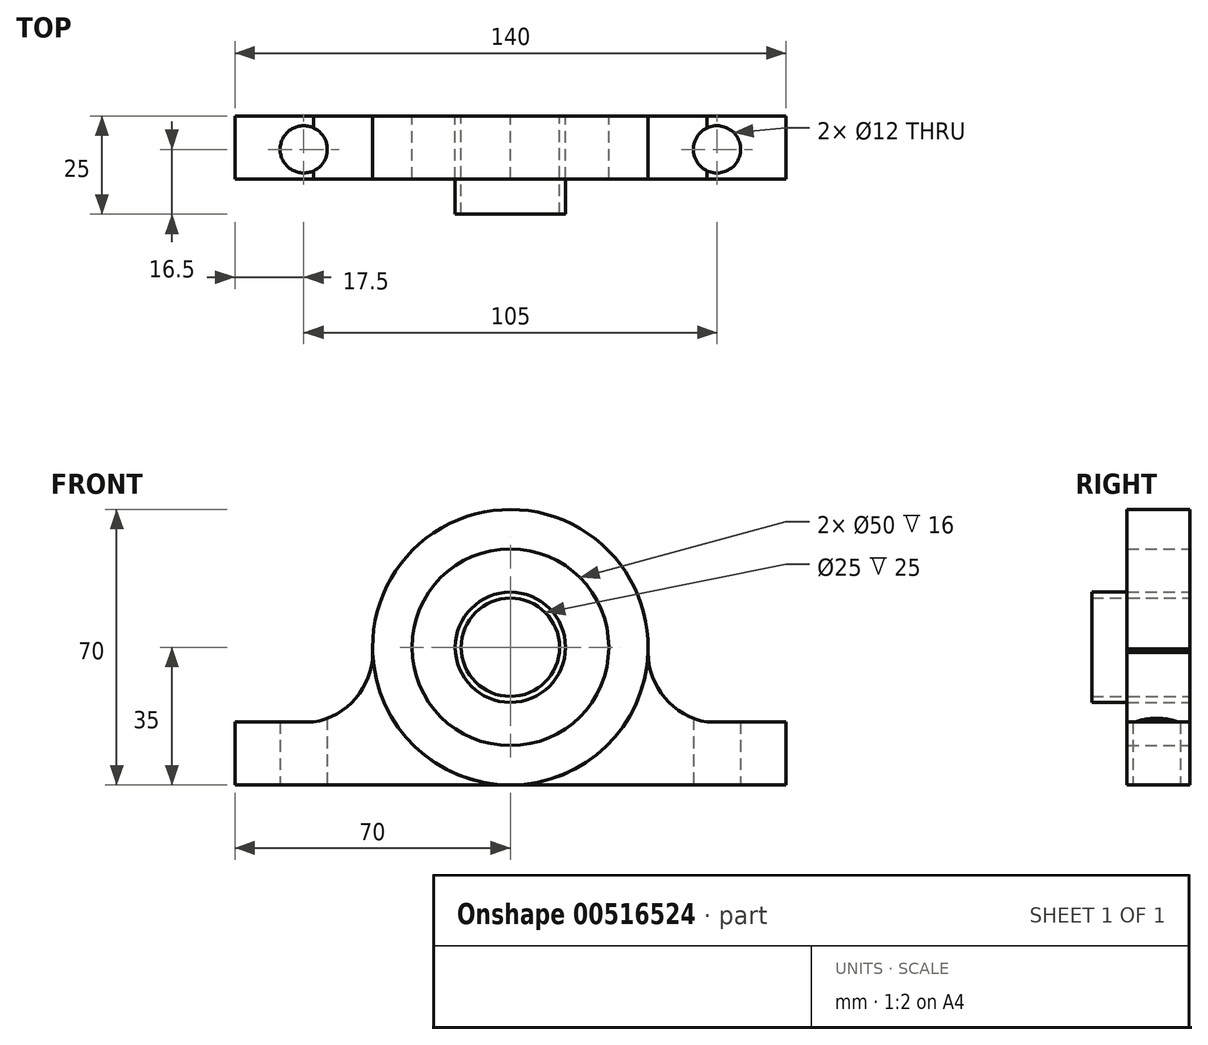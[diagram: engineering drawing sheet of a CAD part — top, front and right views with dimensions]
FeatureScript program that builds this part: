
annotation { "Feature Type Name" : "Feature", "Feature Type Description" : "" }
export const myFeature = defineFeature(function(context is Context, id is Id, definition is map)
    precondition{}
    {
        {
            var Q0;
            Q0=qCreatedBy(makeId("Front.planeOp"),FACE);
            var sketch = newSketch(context, id + "F0", { "sketchPlane" : qUnion([Q0])});
            skLineSegment(sketch, "E0", {"start": v(0, 74.96) * mm, "end": v(0, -75.16) * mm, "construction": true});
            skLineSegment(sketch, "E1", {"start": v(-74.87, 0) * mm, "end": v(74.87, 0) * mm, "construction": true});
            skPoint(sketch, "E2.middle", {"position": v(0, 0) * mm});
            skLineSegment(sketch, "E3.bottom", {"start": v(-70, -8) * mm, "end": v(70, -8) * mm});
            skLineSegment(sketch, "E3.top", {"start": v(-70, 8) * mm, "end": v(70, 8) * mm});
            skLineSegment(sketch, "E3.left", {"start": v(-70, -8) * mm, "end": v(-70, 8) * mm});
            skLineSegment(sketch, "E3.right", {"start": v(70, -8) * mm, "end": v(70, 8) * mm});
            skCircle(sketch, "E4", {"center": v(0, 27) * mm, "radius": 35 * mm});
            skArc(sketch, "E5", {"start": v(-50, 8) * mm, "mid": v(-38.9, 14.54) * mm, "end": v(-35, 26.83) * mm});
            skArc(sketch, "E6", {"start": v(35, 26.62) * mm, "mid": v(38.96, 14.46) * mm, "end": v(50, 8) * mm});
            skCircle(sketch, "E7", {"center": v(0, 27) * mm, "radius": 12.5 * mm});
            skCircle(sketch, "E8", {"center": v(0, 27) * mm, "radius": 14 * mm});
            skCircle(sketch, "E9", {"center": v(0, 27) * mm, "radius": 25 * mm});
            skCircle(sketch, "E10", {"center": v(0, 27) * mm, "radius": 23.5 * mm});
            skSolve(sketch);
        }
        {
            var Q0;
            {var subQ0=sQuery(id+"F0.wireOp",EDGE,"E3.right");Q0=makeQuery(id+"F0.imprint","IMPRINT",FACE,{"disambiguationData":[TD([[makeQuery(id+"F0.imprint","IMPRINT",EDGE,{"derivedFrom":subQ0}),1.0]])]});}
            var Q1;
            {var subQ0=sQuery(id+"F0.wireOp",EDGE,"E3.left");Q1=makeQuery(id+"F0.imprint","IMPRINT",FACE,{"disambiguationData":[TD([[makeQuery(id+"F0.imprint","IMPRINT",EDGE,{"derivedFrom":subQ0}),-1.0]])]});}
            var Q2;
            {var subQ0=sQuery(id+"F0.wireOp",EDGE,"E5");var subQ1=sQuery(id+"F0.wireOp",EDGE,"E3.top");var subQ2=makeQuery(id+"F0.imprint","INTERSECT",VERTEX,{"derivedFrom":[subQ1,subQ0]});Q2=makeQuery(id+"F0.imprint","IMPRINT",FACE,{"disambiguationData":[TD([[makeQuery(id+"F0.imprint","IMPRINT",EDGE,{"disambiguationData":[TD([[subQ2,-1.0]])],"derivedFrom":subQ1}),1.0]])]});}
            var Q3;
            {var subQ0=sQuery(id+"F0.wireOp",EDGE,"E6");var subQ1=sQuery(id+"F0.wireOp",EDGE,"E3.top");var subQ2=makeQuery(id+"F0.imprint","INTERSECT",VERTEX,{"derivedFrom":[subQ1,subQ0]});Q3=makeQuery(id+"F0.imprint","IMPRINT",FACE,{"disambiguationData":[TD([[makeQuery(id+"F0.imprint","IMPRINT",EDGE,{"disambiguationData":[TD([[subQ2,1.0]])],"derivedFrom":subQ1}),1.0]])]});}
            extrude(context, id + "F1", {"entities" : qUnion([Q0, Q1, Q2, Q3]), "depth" : 16 * mm, "offsetDistance" : 25 * mm});
        }
        {
            var Q0;
            {var subQ0=sQuery(id+"F0.wireOp",EDGE,"E4");var subQ2=sQuery(id+"F0.wireOp",EDGE,"E3.top");var subQ4=makeQuery(id+"F0.imprint","INTERSECT",VERTEX,{"disambiguationData":[OD(0.0)],"derivedFrom":[subQ2,subQ0]});Q0=makeQuery(id+"F0.imprint","IMPRINT",FACE,{"disambiguationData":[TD([[makeQuery(id+"F0.imprint","IMPRINT",EDGE,{"disambiguationData":[TD([[subQ4,-1.0]])],"derivedFrom":subQ2}),-1.0]])]});}
            var Q1;
            {var subQ1=sQuery(id+"F0.wireOp",EDGE,"E4");var subQ3=sQuery(id+"F0.wireOp",EDGE,"E3.top");var subQ11=makeQuery(id+"F0.imprint","INTERSECT",VERTEX,{"disambiguationData":[OD(0.0)],"derivedFrom":[subQ3,subQ1]});Q1=makeQuery(id+"F0.imprint","IMPRINT",FACE,{"disambiguationData":[TD([[makeQuery(id+"F0.imprint","IMPRINT",EDGE,{"disambiguationData":[TD([[subQ11,-1.0]])],"derivedFrom":subQ3}),1.0]])]});}
            extrude(context, id + "F2", {"entities" : qUnion([Q0, Q1]), "depth" : 16 * mm, "offsetDistance" : 25 * mm});
        }
        {
            var Q0;
            {var subQ0=sQuery(id+"F0.wireOp",EDGE,"E9");var subQ1=sQuery(id+"F0.wireOp",EDGE,"E3.top");var subQ2=makeQuery(id+"F0.imprint","INTERSECT",VERTEX,{"disambiguationData":[OD(0.0)],"derivedFrom":[subQ1,subQ0]});Q0=makeQuery(id+"F0.imprint","IMPRINT",FACE,{"disambiguationData":[TD([[makeQuery(id+"F0.imprint","IMPRINT",EDGE,{"disambiguationData":[TD([[subQ2,-1.0]])],"derivedFrom":subQ1}),1.0]])]});}
            var Q1;
            {var subQ0=sQuery(id+"F0.wireOp",EDGE,"E9");var subQ1=sQuery(id+"F0.wireOp",EDGE,"E3.top");var subQ2=makeQuery(id+"F0.imprint","INTERSECT",VERTEX,{"disambiguationData":[OD(0.0)],"derivedFrom":[subQ1,subQ0]});Q1=makeQuery(id+"F0.imprint","IMPRINT",FACE,{"disambiguationData":[TD([[makeQuery(id+"F0.imprint","IMPRINT",EDGE,{"disambiguationData":[TD([[subQ2,-1.0]])],"derivedFrom":subQ1}),-1.0]])]});}
            extrude(context, id + "F3", {"entities" : qUnion([Q0, Q1]), "depth" : 16 * mm, "offsetDistance" : 25 * mm});
        }
        {
            var Q0;
            Q0=makeQuery(id+"F0.imprint","IMPRINT",FACE,{"disambiguationData":[TD([[makeQuery(id+"F0.imprint","IMPRINT",EDGE,{"derivedFrom":sQuery(id+"F0.wireOp",EDGE,"E7")}),-1.0]])]});
            extrude(context, id + "F4", {"entities" : qUnion([Q0]), "depth" : 25 * mm, "offsetDistance" : 25 * mm});
        }
        {
            var Q0;
            {var subQ0=sQuery(id+"F0.wireOp",EDGE,"E3.bottom");Q0=makeQuery(id+"F1.opExtrude","SWEPT_FACE",FACE,{"disambiguationData":[OSD([subQ0]),TDD([makeQuery(id+"F0.imprint","IMPRINT",EDGE,{"disambiguationData":[TD([[makeQuery(id+"F0.imprint","INTERSECT",VERTEX,{"derivedFrom":[subQ0,sQuery(id+"F0.wireOp",EDGE,"E3.right")]}),1.0]])],"derivedFrom":subQ0})])]});}
            var sketch = newSketch(context, id + "F5", { "sketchPlane" : qUnion([Q0])});
            skLineSegment(sketch, "E11", {"start": v(-52.5, 8.5) * mm, "end": v(52.5, 8.5) * mm, "construction": true});
            skCircle(sketch, "E12", {"center": v(-52.5, 8.5) * mm, "radius": 6 * mm});
            skCircle(sketch, "E13", {"center": v(52.5, 8.5) * mm, "radius": 6 * mm});
            skSolve(sketch);
        }
        {
            var Q0;
            Q0=makeQuery(id+"F5.imprint","IMPRINT",FACE,{"disambiguationData":[TD([[makeQuery(id+"F5.imprint","IMPRINT",EDGE,{"derivedFrom":sQuery(id+"F5.wireOp",EDGE,"E12")}),1.0]])]});
            var Q1;
            Q1=makeQuery(id+"F5.imprint","IMPRINT",FACE,{"disambiguationData":[TD([[makeQuery(id+"F5.imprint","IMPRINT",EDGE,{"derivedFrom":sQuery(id+"F5.wireOp",EDGE,"E13")}),1.0]])]});
            extrude(context, id + "F6", {"entities" : qUnion([Q0, Q1]), "operationType" : NewBodyOperationType.REMOVE, "endBound" : BoundingType.THROUGH_ALL, "oppositeDirection" : true, "depth" : 25 * mm, "offsetDistance" : 25 * mm});
        }
    });
